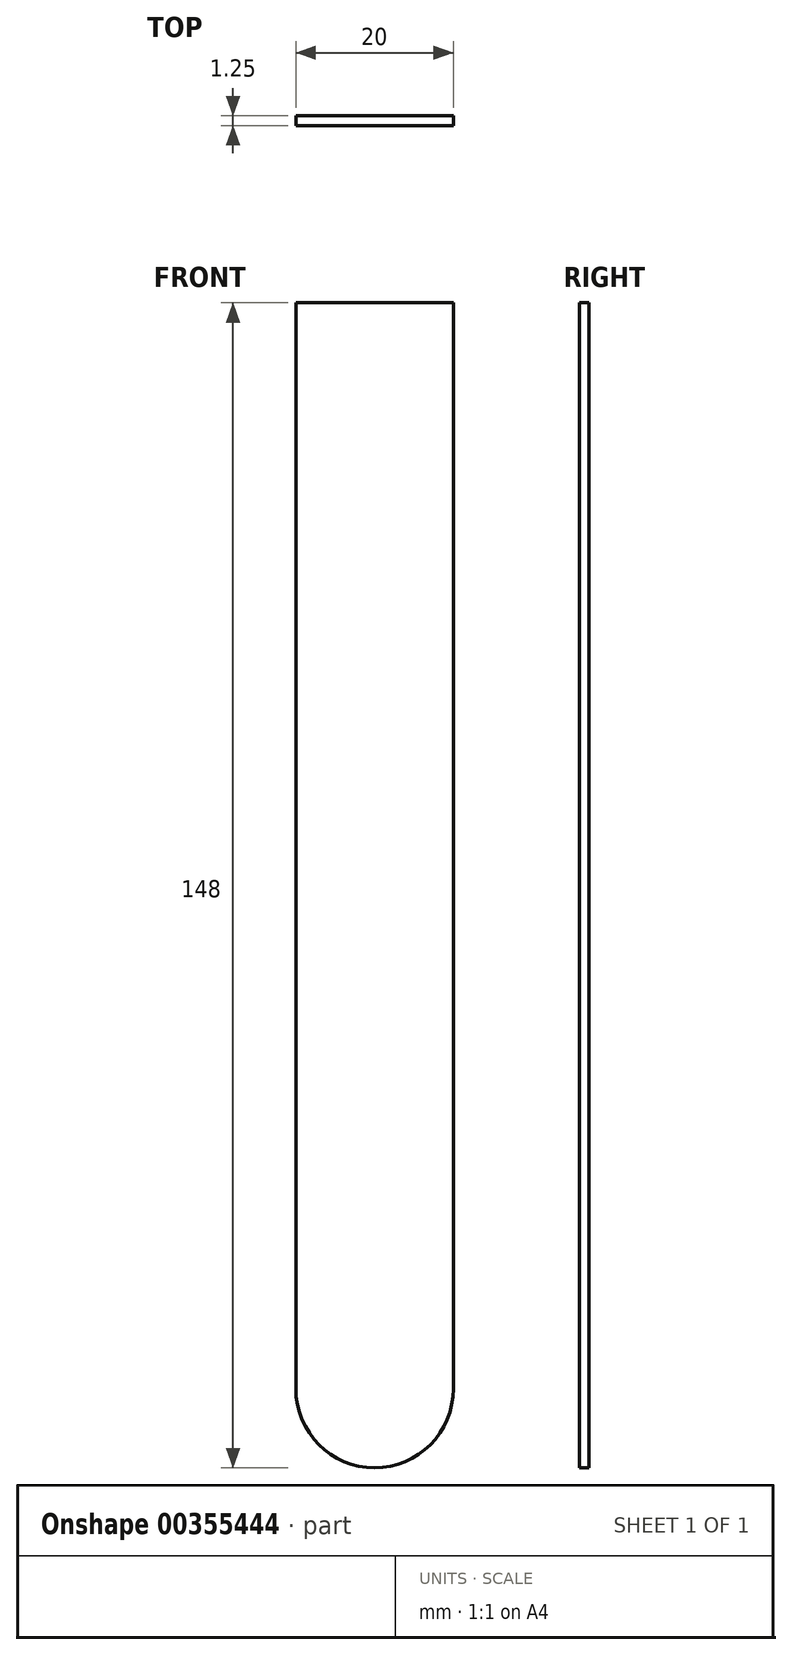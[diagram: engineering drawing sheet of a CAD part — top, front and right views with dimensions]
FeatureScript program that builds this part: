
annotation { "Feature Type Name" : "Feature", "Feature Type Description" : "" }
export const myFeature = defineFeature(function(context is Context, id is Id, definition is map)
    precondition{}
    {
        {
            var Q0;
            Q0=qCreatedBy(makeId("Front.planeOp"),FACE);
            var sketch = newSketch(context, id + "F0", { "sketchPlane" : qUnion([Q0])});
            skLineSegment(sketch, "E0.bottom", {"start": v(-10, 69) * mm, "end": v(10, 69) * mm});
            skLineSegment(sketch, "E0.top", {"start": v(-10, -69) * mm, "end": v(10, -69) * mm});
            skLineSegment(sketch, "E0.left", {"start": v(-10, 69) * mm, "end": v(-10, -69) * mm});
            skLineSegment(sketch, "E0.right", {"start": v(10, 69) * mm, "end": v(10, -69) * mm});
            skPoint(sketch, "E0.middle", {"position": v(0, 0) * mm});
            skArc(sketch, "E1", {"start": v(-10, -69) * mm, "mid": v(0, -79) * mm, "end": v(10, -69) * mm});
            skSolve(sketch);
        }
        {
            var Q0;
            Q0=qSketchRegion(id+"F0",true);
            extrude(context, id + "F1", {"entities" : qUnion([Q0]), "depth" : 1.25 * mm});
        }
    });
